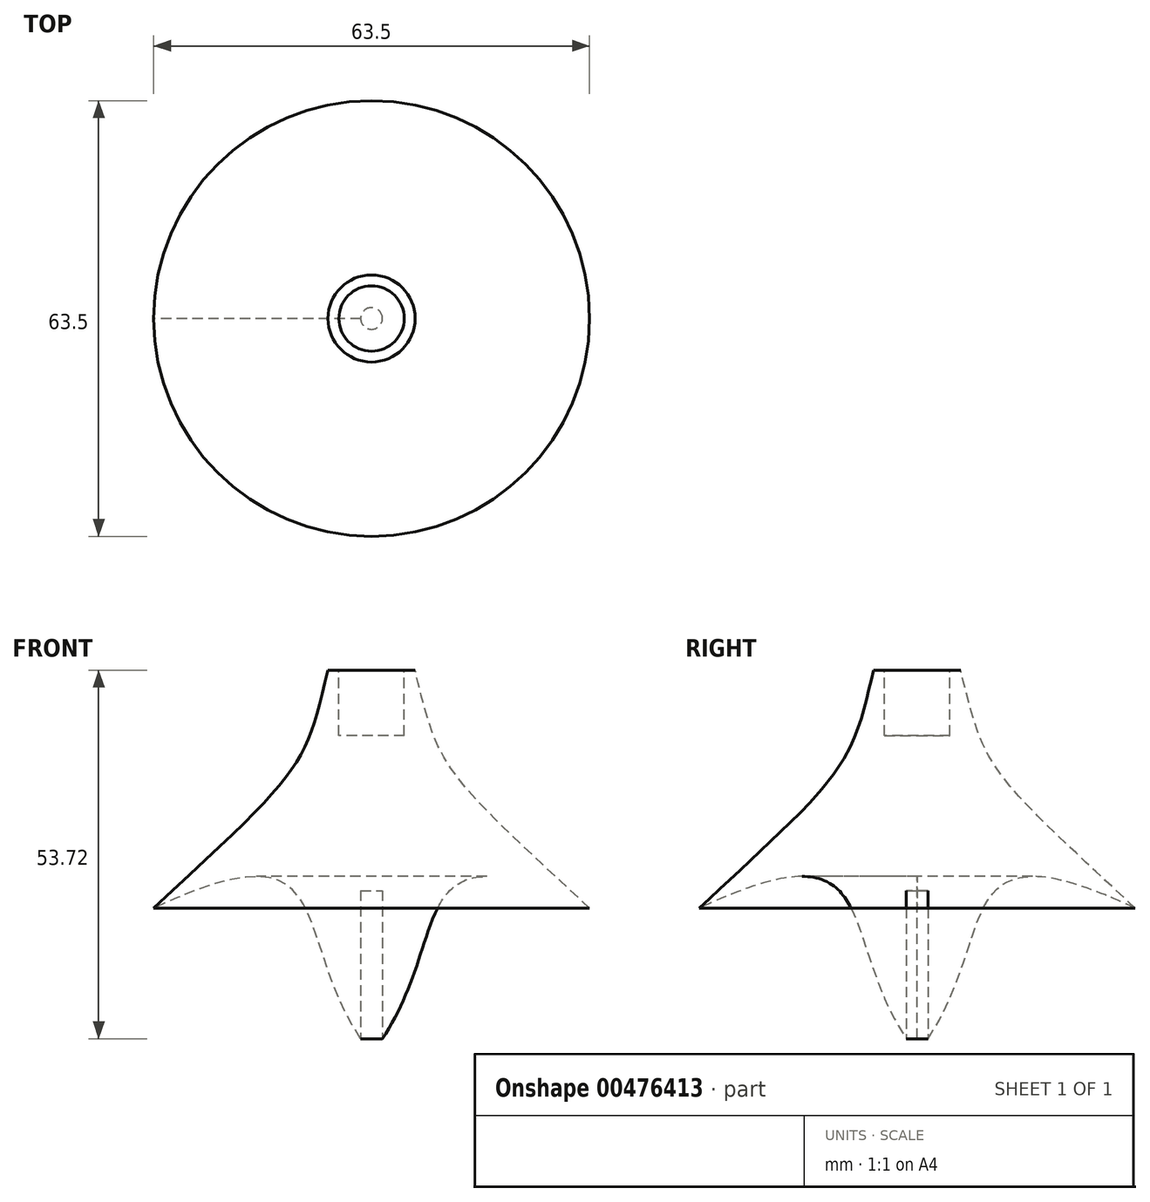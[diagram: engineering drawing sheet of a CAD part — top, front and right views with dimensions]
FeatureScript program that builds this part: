
annotation { "Feature Type Name" : "Feature", "Feature Type Description" : "" }
export const myFeature = defineFeature(function(context is Context, id is Id, definition is map)
    precondition{}
    {
        {
            var Q0;
            Q0=qCreatedBy(makeId("Front.planeOp"),FACE);
            var sketch = newSketch(context, id + "F0", { "sketchPlane" : qUnion([Q0])});
            skLineSegment(sketch, "E0.bottom", {"start": v(31.75, 31.75) * mm, "end": v(-31.75, 31.75) * mm});
            skLineSegment(sketch, "E0.top", {"start": v(31.75, -31.75) * mm, "end": v(-31.75, -31.75) * mm});
            skLineSegment(sketch, "E0.left", {"start": v(31.75, 31.75) * mm, "end": v(31.75, -31.75) * mm});
            skLineSegment(sketch, "E0.right", {"start": v(-31.75, 31.75) * mm, "end": v(-31.75, -31.75) * mm});
            skPoint(sketch, "E0.middle", {"position": v(0, 0) * mm});
            skLineSegment(sketch, "E1", {"start": v(0, -31.75) * mm, "end": v(0, 31.75) * mm});
            skPoint(sketch, "E2", {"position": v(31.75, -12.7) * mm});
            skLineSegment(sketch, "E3", {"start": v(0, -31.75) * mm, "end": v(1.59, -31.75) * mm});
            skLineSegment(sketch, "E4", {"start": v(0, 31.75) * mm, "end": v(6.35, 31.75) * mm});
            skLineSegment(sketch, "E5", {"start": v(1.59, -31.75) * mm, "end": v(1.59, -10.16) * mm});
            skLineSegment(sketch, "E6", {"start": v(1.59, -10.16) * mm, "end": v(0, -10.16) * mm});
            skLineSegment(sketch, "E7", {"start": v(6.35, 31.75) * mm, "end": v(6.35, 21.97) * mm});
            skLineSegment(sketch, "E8", {"start": v(6.35, 21.97) * mm, "end": v(0, 21.97) * mm});
            skLineSegment(sketch, "E9", {"start": v(1.59, -31.75) * mm, "end": v(31.75, -31.75) * mm});
            skPoint(sketch, "E10", {"position": v(16.67, -31.75) * mm});
            skFitSpline(sketch, "E11", {"points": [v(1.59, -31.75) * mm, v(31.75, -12.7) * mm], "startDerivative": vector(31.17, 47.11) * mm, "endDerivative": vector(82.24, -38.1) * mm});
            skFitSpline(sketch, "E12", {"points": [v(6.35, 21.97) * mm, v(31.75, -12.7) * mm], "startDerivative": vector(10.29, -43.02) * mm, "endDerivative": vector(65.91, -61) * mm});
            skSolve(sketch);
        }
        {
            var Q0;
            Q0=makeQuery(id+"F0.imprint","IMPRINT",FACE,{"disambiguationData":[TD([[makeQuery(id+"F0.imprint","IMPRINT",EDGE,{"derivedFrom":sQuery(id+"F0.wireOp",EDGE,"E5")}),-1.0]])]});
            var Q1;
            Q1=sQuery(id+"F0.wireOp",EDGE,"E1");
            revolve(context, id + "F1", {"entities" : qUnion([Q0]), "axis" : qUnion([Q1]), "revolveType" : RevolveType.FULL});
        }
        {
            var Q0;
            Q0=makeQuery(id+"F1.opRevolve","SWEPT_FACE",FACE,{"disambiguationData":[OSD([sQuery(id+"F0.wireOp",EDGE,"E8")])]});
            var sketch = newSketch(context, id + "F2", { "sketchPlane" : qUnion([Q0])});
            skCircle(sketch, "E13", {"center": v(0, 0) * mm, "radius": 4.76 * mm});
            skSolve(sketch);
        }
        {
            var Q0;
            Q0=makeQuery(id+"F2.imprint","IMPRINT",FACE,{"disambiguationData":[TD([[makeQuery(id+"F2.imprint","IMPRINT",EDGE,{"derivedFrom":sQuery(id+"F2.wireOp",EDGE,"E13")}),1.0]])]});
            extrude(context, id + "F3", {"entities" : qUnion([Q0]), "operationType" : NewBodyOperationType.REMOVE, "oppositeDirection" : true, "depth" : 9.52 * mm});
        }
    });
